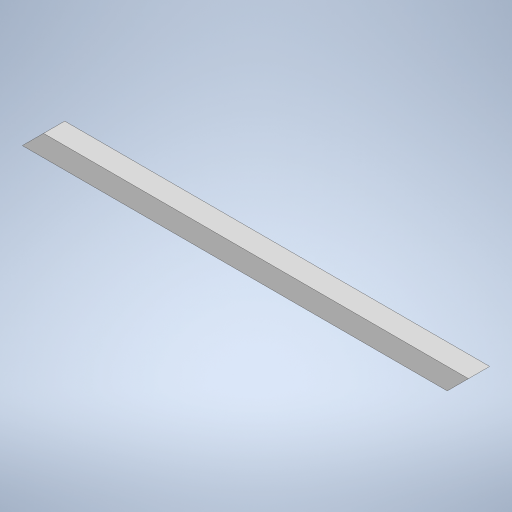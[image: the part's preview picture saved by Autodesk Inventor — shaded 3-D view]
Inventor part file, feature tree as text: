
AUTODESK INVENTOR PART (.ipt)
format: ipt  version: 2024.3 (Build 283343000, 343)  size: 247,808 bytes
history: native  units: mm
features: extrude x2, sketch x2
ambient origin geometry x8: Origin, YZ Plane, XZ Plane, XY Plane, X Axis, Y Axis, Z Axis, Center Point
bodies: Solid1 (feature_tree)
feature tree (4):
  extrude  "Extrusion1"  Depth=2.0mm
  extrude  "Extrusion2"  Depth=19.0mm
  sketch  "Sketch1"  dims[d0=2.0mm d1=2.0mm]
  sketch  "Sketch2"  dims[d2=19.0mm d3=19.0mm d4=400.0mm d5=0.0mm d6=19.0mm d7=19.0mm d8=0.0mm d9=0.0mm]
